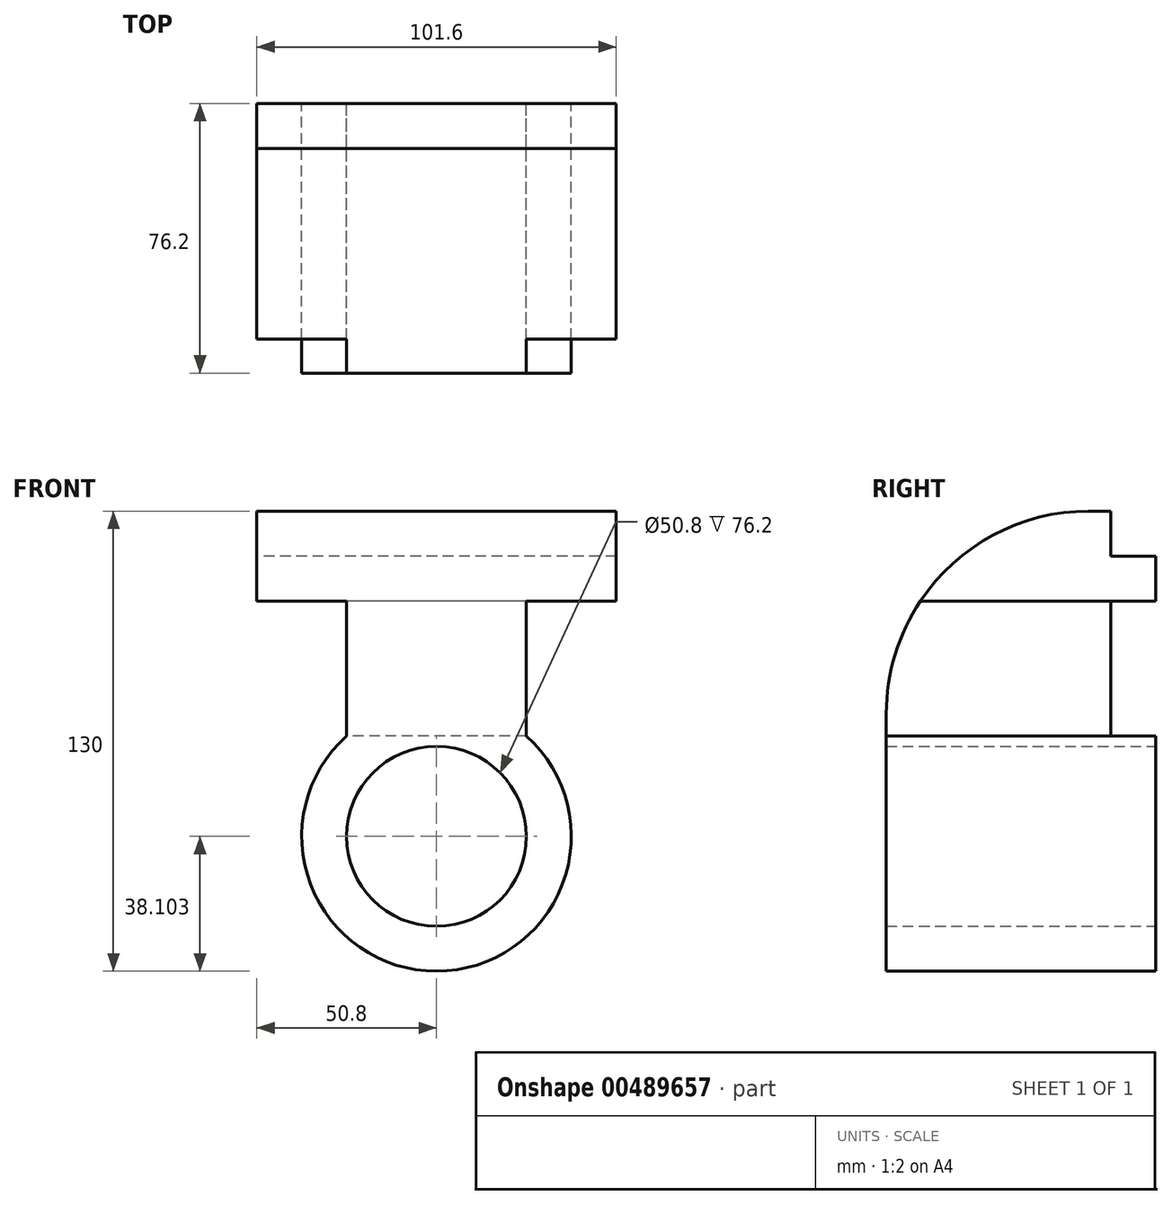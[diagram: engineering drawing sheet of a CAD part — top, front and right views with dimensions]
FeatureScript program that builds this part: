
annotation { "Feature Type Name" : "Feature", "Feature Type Description" : "" }
export const myFeature = defineFeature(function(context is Context, id is Id, definition is map)
    precondition{}
    {
        {
            var Q0;
            Q0=qCreatedBy(makeId("Front.planeOp"),FACE);
            var sketch = newSketch(context, id + "F0", { "sketchPlane" : qUnion([Q0])});
            skLineSegment(sketch, "E0.bottom", {"start": v(50.8, 12.7) * mm, "end": v(-50.8, 12.7) * mm});
            skLineSegment(sketch, "E0.top", {"start": v(50.8, -12.7) * mm, "end": v(25.4, -12.7) * mm});
            skLineSegment(sketch, "E0.left", {"start": v(50.8, 12.7) * mm, "end": v(50.8, -12.7) * mm});
            skLineSegment(sketch, "E0.right", {"start": v(-50.8, 12.7) * mm, "end": v(-50.8, -12.7) * mm});
            skPoint(sketch, "E0.middle", {"position": v(0, 0) * mm});
            skPoint(sketch, "E1.endSnap0", {"position": v(0, -12.7) * mm});
            skCircle(sketch, "E2", {"center": v(0, -79.2) * mm, "radius": 25.4 * mm});
            skCircle(sketch, "E3", {"center": v(0, -79.2) * mm, "radius": 38.1 * mm});
            skLineSegment(sketch, "E4.left", {"start": v(25.4, -12.7) * mm, "end": v(25.4, -50.8) * mm});
            skLineSegment(sketch, "E4.right", {"start": v(-25.4, -12.7) * mm, "end": v(-25.4, -50.8) * mm});
            skLineSegment(sketch, "E5.trimOffspring", {"start": v(-25.4, -12.7) * mm, "end": v(-50.8, -12.7) * mm});
            skSolve(sketch);
        }
        {
            var Q0;
            Q0 = qSketchRegion(id + "F0", true);
            extrude(context, id + "F1", {"entities" : qUnion([Q0]), "depth" : 76.2 * mm});
        }
        {
            var Q0;
            Q0=makeQuery(id+"F1.opExtrude","SWEPT_FACE",FACE,{"disambiguationData":[OSD([sQuery(id+"F0.wireOp",EDGE,"E0.right")])]});
            var sketch = newSketch(context, id + "F2", { "sketchPlane" : qUnion([Q0])});
            skLineSegment(sketch, "E6", {"start": v(0, 0) * mm, "end": v(12.7, 0) * mm});
            skLineSegment(sketch, "E7", {"start": v(12.7, 0) * mm, "end": v(12.7, 12.7) * mm});
            skLineSegment(sketch, "E8", {"start": v(76.2, 12.7) * mm, "end": v(25.4, 12.7) * mm});
            skLineSegment(sketch, "E9", {"start": v(25.4, 12.7) * mm, "end": v(25.4, -12.7) * mm});
            skLineSegment(sketch, "E10", {"start": v(25.4, -12.7) * mm, "end": v(76.2, -12.7) * mm});
            skLineSegment(sketch, "E11", {"start": v(76.2, -12.7) * mm, "end": v(76.2, 12.7) * mm});
            skLineSegment(sketch, "E12", {"start": v(76.2, 12.7) * mm, "end": v(76.2, -50.8) * mm});
            skSolve(sketch);
        }
        {
            var Q0;
            {var subQ0=sQuery(id+"F2.wireOp",EDGE,"E6");Q0=makeQuery(id+"F2.imprint","IMPRINT",FACE,{"disambiguationData":[TD([[makeQuery(id+"F2.imprint","IMPRINT",EDGE,{"derivedFrom":subQ0}),1.0]])]});}
            extrude(context, id + "F3", {"entities" : qUnion([Q0]), "operationType" : NewBodyOperationType.REMOVE, "endBound" : BoundingType.THROUGH_ALL, "oppositeDirection" : true, "depth" : 25.4 * mm});
        }
        {
            var Q0;
            Q0=makeQuery(id+"F1.opExtrude","CAP_EDGE",EDGE,{"disambiguationData":[OSD([sQuery(id+"F0.wireOp",EDGE,"E0.bottom")])],"isStart":false});
            fillet(context, id + "F4", {"entities" : qUnion([Q0]), "radius" : 57.15 * mm, "tangentPropagation" : true, "allowEdgeOverflow" : false});
        }
        {
            var Q0;
            Q0=makeQuery(id+"F1.opExtrude","SWEPT_FACE",FACE,{"disambiguationData":[OSD([sQuery(id+"F0.wireOp",EDGE,"E4.right")])]});
            var sketch = newSketch(context, id + "F5", { "sketchPlane" : qUnion([Q0])});
            skLineSegment(sketch, "E13.bottom", {"start": v(0, -12.7) * mm, "end": v(12.7, -12.7) * mm});
            skLineSegment(sketch, "E13.top", {"start": v(0, -50.8) * mm, "end": v(12.7, -50.8) * mm});
            skLineSegment(sketch, "E13.left", {"start": v(0, -12.7) * mm, "end": v(0, -50.8) * mm});
            skLineSegment(sketch, "E13.right", {"start": v(12.7, -12.7) * mm, "end": v(12.7, -50.8) * mm});
            skSolve(sketch);
        }
        {
            var Q0;
            Q0 = qSketchRegion(id + "F5", true);
            extrude(context, id + "F6", {"entities" : qUnion([Q0]), "operationType" : NewBodyOperationType.REMOVE, "endBound" : BoundingType.THROUGH_ALL, "oppositeDirection" : true, "depth" : 25.4 * mm});
        }
    });
